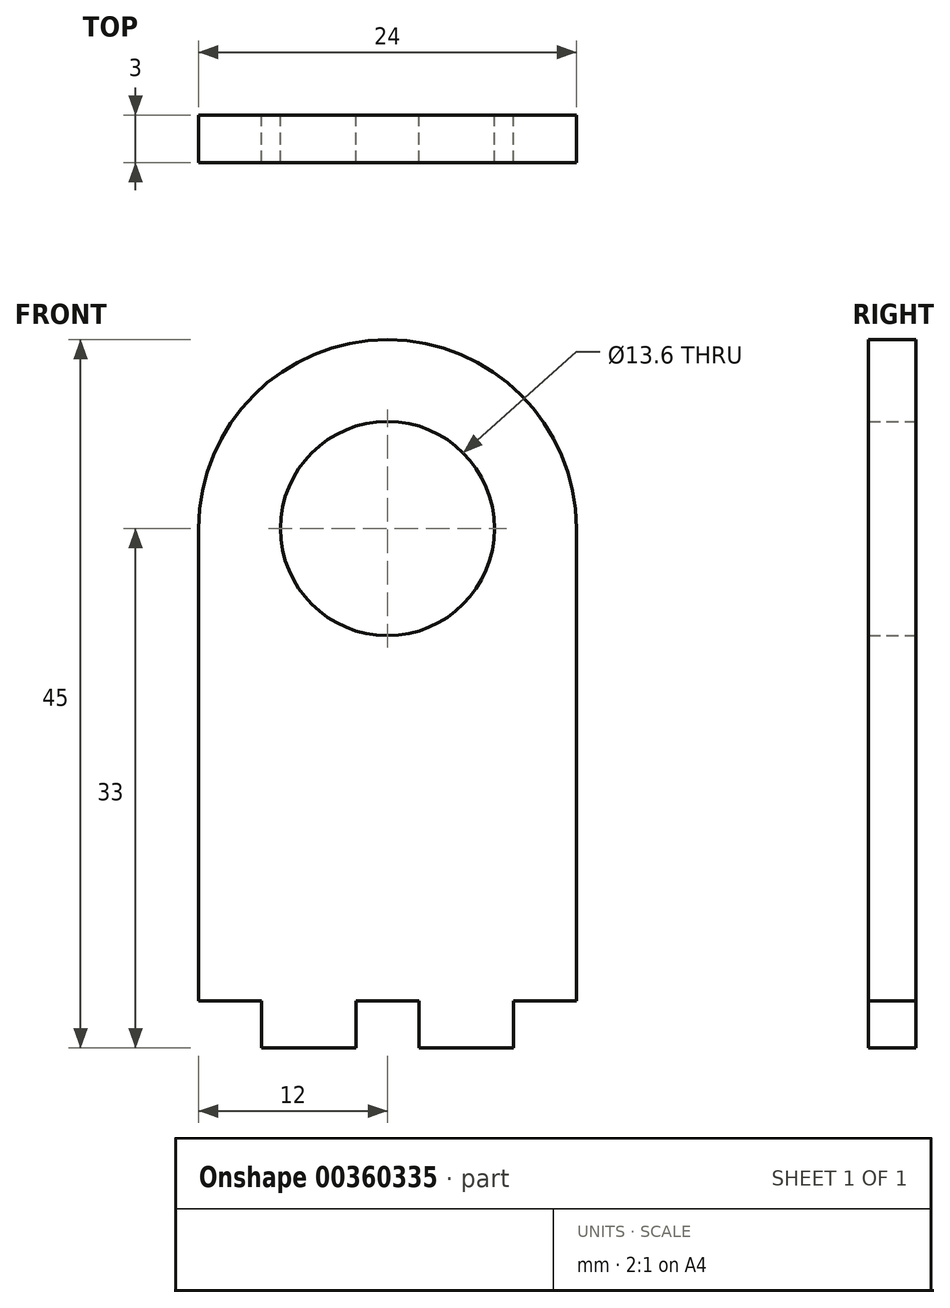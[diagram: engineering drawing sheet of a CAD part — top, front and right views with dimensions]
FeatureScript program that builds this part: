
annotation { "Feature Type Name" : "Feature", "Feature Type Description" : "" }
export const myFeature = defineFeature(function(context is Context, id is Id, definition is map)
    precondition{}
    {
        {
            var Q0;
            Q0=qCreatedBy(makeId("Front.planeOp"),FACE);
            var sketch = newSketch(context, id + "F0", { "sketchPlane" : qUnion([Q0])});
            skLineSegment(sketch, "E0", {"start": v(0, 0) * mm, "end": v(-2, 0) * mm});
            skLineSegment(sketch, "E1", {"start": v(-2, 0) * mm, "end": v(-2, -3) * mm});
            skLineSegment(sketch, "E2", {"start": v(-2, -3) * mm, "end": v(-8, -3) * mm});
            skLineSegment(sketch, "E3", {"start": v(-8, -3) * mm, "end": v(-8, 0) * mm});
            skLineSegment(sketch, "E4", {"start": v(-8, 0) * mm, "end": v(-12, 0) * mm});
            skLineSegment(sketch, "E5", {"start": v(-12, 0) * mm, "end": v(-12, 30) * mm});
            skArc(sketch, "E6", {"start": v(-12, 30) * mm, "mid": v(-8.49, 38.49) * mm, "end": v(0, 42) * mm});
            skArc(sketch, "E7", {"start": v(0, 36.8) * mm, "mid": v(-6.8, 30) * mm, "end": v(0, 23.2) * mm});
            skLineSegment(sketch, "E8.MirrorCS", {"start": v(8, -3) * mm, "end": v(8, 0) * mm});
            skLineSegment(sketch, "E9.MirrorCS", {"start": v(8, 0) * mm, "end": v(12, 0) * mm});
            skLineSegment(sketch, "E10.MirrorCS", {"start": v(2, 0) * mm, "end": v(2, -3) * mm});
            skLineSegment(sketch, "E11.MirrorCS", {"start": v(0, 0) * mm, "end": v(2, 0) * mm});
            skLineSegment(sketch, "E12.MirrorCS", {"start": v(12, 0) * mm, "end": v(12, 30) * mm});
            skLineSegment(sketch, "E13.MirrorCS", {"start": v(2, -3) * mm, "end": v(8, -3) * mm});
            skArc(sketch, "E14.MirrorCS", {"start": v(0, 36.8) * mm, "mid": v(6.8, 30) * mm, "end": v(0, 23.2) * mm});
            skArc(sketch, "E15.MirrorCS", {"start": v(12, 30) * mm, "mid": v(8.49, 38.49) * mm, "end": v(0, 42) * mm});
            skSolve(sketch);
        }
        {
            var Q0;
            Q0 = qSketchRegion(id + "F0", true);
            extrude(context, id + "F1", {"entities" : qUnion([Q0]), "depth" : 3 * mm});
        }
    });
